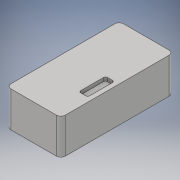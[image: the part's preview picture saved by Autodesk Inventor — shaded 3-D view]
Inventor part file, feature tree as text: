
AUTODESK INVENTOR PART (.ipt)
format: ipt  version: 2018 (Build 220112000, 112)  size: 176,128 bytes
history: native  units: in
note: dims shown in document units (in); Inventor stores cm internally (conversion verified against a paired STEP export)
features: sketch x8, extrude x6, fillet x4
ambient origin geometry x8: Origin, YZ Plane, XZ Plane, XY Plane, X Axis, Y Axis, Z Axis, Center Point
bodies: Solid1 (feature_tree)
feature tree (18):
  extrude  "Extrusion1"  Depth=3.17in
  fillet  "Fillet1"  Radius=1.0in
  extrude  "Extrusion2"  Depth=0.93in
  fillet  "Fillet2"  Radius=2.4in
  fillet  "Fillet3"  Radius=0.1in
  extrude  "Extrusion4"  Depth=0.25in TaperAngle=0.0deg
  sketch  "Sketch8"  dims[d20=0.1in d21=0.0in d27=0.0in d28=0.1in]
  sketch  "Sketch9"  dims[d29=0.5in]
  extrude  "Extrusion6"  Depth=0.05in
  fillet  "Fillet4"  Radius=0.15in
  sketch  "Sketch2"  dims[d0=1.53in d1=3.17in d2=1.0in d3=0.0in]
  sketch  "Sketch3"  dims[d4=0.125in d5=0.93in d6=2.4in d7=0.1in d8=0.0in]
  sketch  "Sketch6"  dims[d15=0.05in d16=0.15in d17=0.15in]
  sketch  "Sketch10"  dims[d30=0.4in d31=0.0in d32=0.05in]
  sketch  "Sketch4"  dims[d9=0.06in d10=0.25in d11=0.75in d13=0.0in d14=0.1in]
  sketch  "Sketch7"  dims[d18=0.15in d19=0.15in]
  extrude  "Extrusion3"  Depth=0.15in
  extrude  "Extrusion5"  Depth=0.1in TaperAngle=0.0deg
